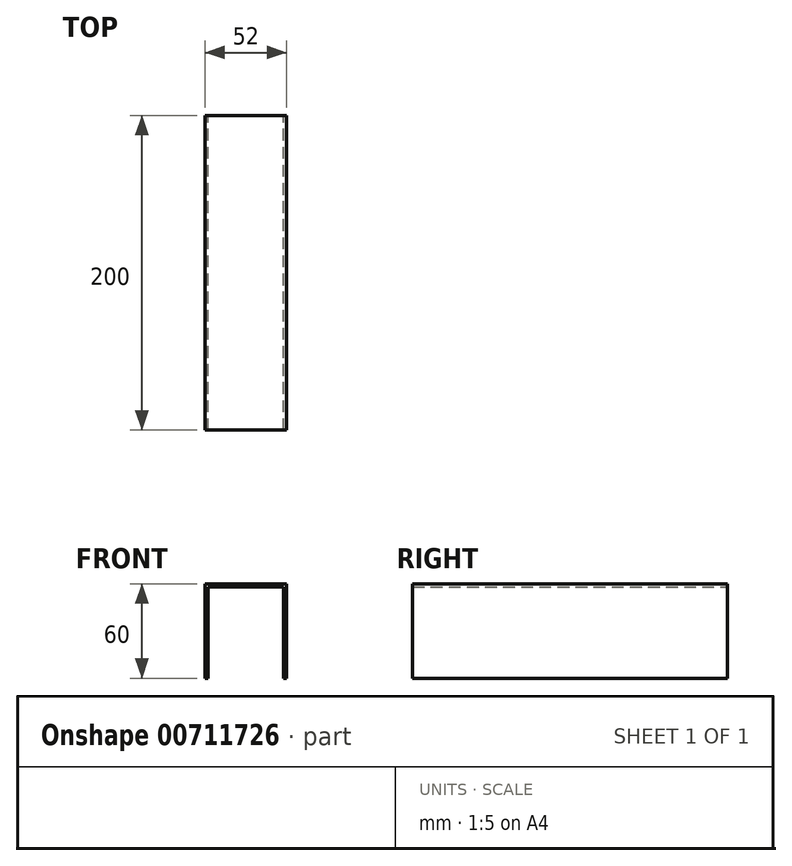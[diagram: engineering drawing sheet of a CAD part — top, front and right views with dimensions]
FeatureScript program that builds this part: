
annotation { "Feature Type Name" : "Feature", "Feature Type Description" : "" }
export const myFeature = defineFeature(function(context is Context, id is Id, definition is map)
    precondition{}
    {
        {
            var Q0;
            Q0=qCreatedBy(makeId("Front.planeOp"),FACE);
            var sketch = newSketch(context, id + "F0", { "sketchPlane" : qUnion([Q0])});
            skLineSegment(sketch, "E0.bottom", {"start": v(26, 30) * mm, "end": v(-26, 30) * mm});
            skLineSegment(sketch, "E0.top", {"start": v(26, -30) * mm, "end": v(24, -30) * mm});
            skLineSegment(sketch, "E0.left", {"start": v(26, 30) * mm, "end": v(26, -30) * mm});
            skLineSegment(sketch, "E0.right", {"start": v(-26, 30) * mm, "end": v(-26, -30) * mm});
            skPoint(sketch, "E0.middle", {"position": v(0, 0) * mm});
            skLineSegment(sketch, "E1", {"start": v(-24, -30) * mm, "end": v(-24, 28) * mm});
            skLineSegment(sketch, "E2", {"start": v(-24, 28) * mm, "end": v(24, 28) * mm});
            skLineSegment(sketch, "E3", {"start": v(24, 28) * mm, "end": v(24, -30) * mm});
            skLineSegment(sketch, "E4", {"start": v(24, -30) * mm, "end": v(26, -30) * mm});
            skLineSegment(sketch, "E5", {"start": v(-24, -30) * mm, "end": v(-26, -30) * mm});
            skSolve(sketch);
        }
        {
            var Q0;
            Q0=makeQuery(id+"F0.imprint","IMPRINT",FACE,{"disambiguationData":[TD([[makeQuery(id+"F0.imprint","IMPRINT",EDGE,{"derivedFrom":sQuery(id+"F0.wireOp",EDGE,"E0.bottom")}),1.0]])]});
            extrude(context, id + "F1", {"entities" : qUnion([Q0]), "depth" : 200 * mm, "offsetDistance" : 25 * mm});
        }
    });
